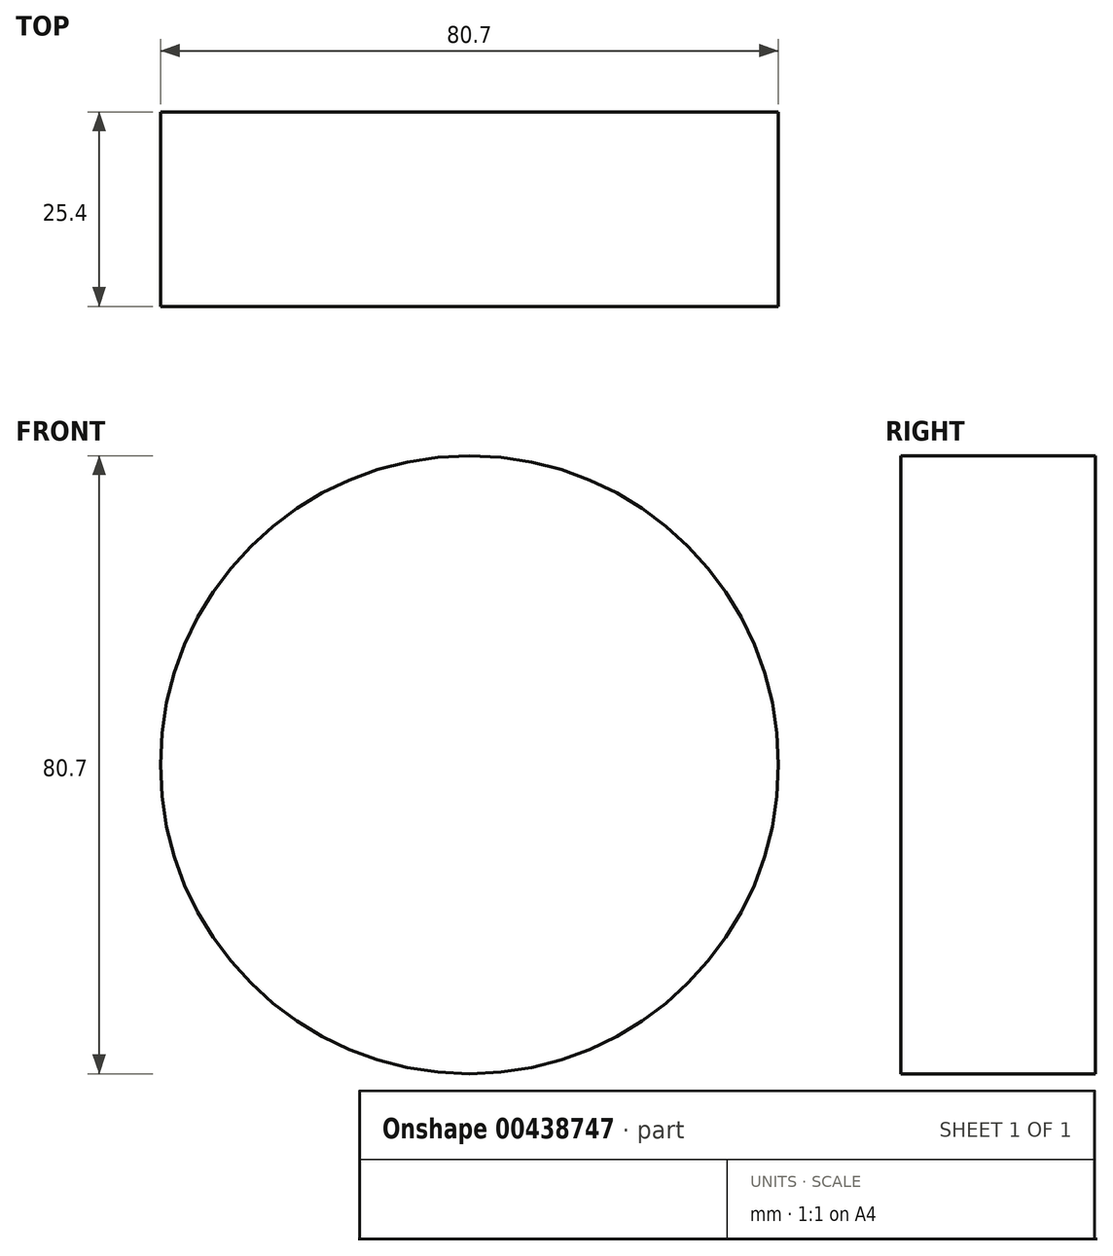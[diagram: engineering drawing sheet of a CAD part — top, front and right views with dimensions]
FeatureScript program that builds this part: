
annotation { "Feature Type Name" : "Feature", "Feature Type Description" : "" }
export const myFeature = defineFeature(function(context is Context, id is Id, definition is map)
    precondition{}
    {
        {
            var Q0;
            Q0=qCreatedBy(makeId("Front.planeOp"),FACE);
            var sketch = newSketch(context, id + "F0", { "sketchPlane" : qUnion([Q0])});
            skCircle(sketch, "E0", {"center": v(4.4, -40.11) * mm, "radius": 40.35 * mm});
            skPoint(sketch, "E0.first.point", {"position": v(0, 0) * mm});
            skPoint(sketch, "E0.second.point", {"position": v(8.78, 0) * mm});
            skPoint(sketch, "E0.third.point", {"position": v(25.68, -5.84) * mm});
            skSolve(sketch);
        }
        {
            var Q0;
            Q0 = qSketchRegion(id + "F0", true);
            extrude(context, id + "F1", {"entities" : qUnion([Q0]), "depth" : 25.4 * mm, "offsetDistance" : 25.4 * mm});
        }
    });
